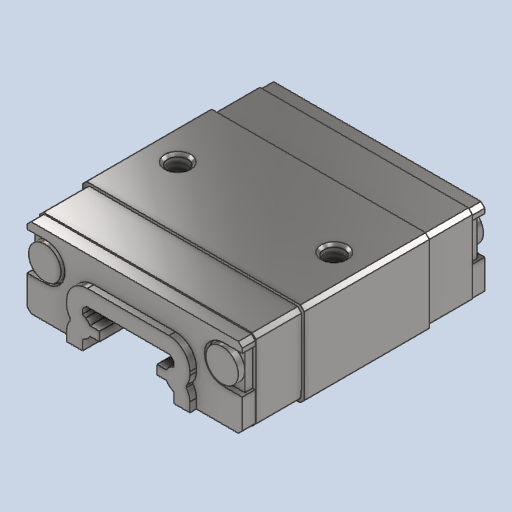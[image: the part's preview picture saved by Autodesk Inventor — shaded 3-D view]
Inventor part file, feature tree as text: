
AUTODESK INVENTOR PART (.ipt)
format: ipt  version: 2023 (Build 270158000, 158)  size: 541,184 bytes
history: native  units: mm
features: sketch x21, extrude x16, other x7, revolve x4, hole x1, pattern_linear x1
ambient origin geometry x8: Origin, YZ Plane, XZ Plane, XY Plane, X Axis, Y Axis, Z Axis, Center Point
bodies: Solid1 (feature_tree)
feature tree (50):
  extrude  "Extrusion1"  Depth=5.0mm TaperAngle=0.0deg
  extrude  "Extrusion2"  Depth=1.5mm TaperAngle=0.0deg
  extrude  "Extrusion3"  Depth=1.5mm TaperAngle=0.0deg
  extrude  "Extrusion4"  Depth=0.6mm TaperAngle=0.0deg
  extrude  "Extrusion5"  Depth=0.6mm TaperAngle=0.0deg
  extrude  "Extrusion6"  TaperAngle=360.0deg  [1 undecoded]
  extrude  "Extrusion7"  TaperAngle=360.0deg  [1 undecoded]
  extrude  "Extrusion8"  Depth=9.6mm TaperAngle=0.0deg
  extrude  "Extrusion9"  Depth=0.05mm TaperAngle=0.0deg
  extrude  "Extrusion10"  Depth=0.05mm TaperAngle=0.0deg
  extrude  "Extrusion11"  Depth=12.0mm TaperAngle=0.0deg
  revolve  "Revolution1"  [1 undecoded]
  revolve  "Revolution2"  [1 undecoded]
  revolve  "Revolution3"  [1 undecoded]
  revolve  "Revolution4"  [1 undecoded]
  extrude  "Extrusion12"  [1 undecoded]
  extrude  "Extrusion13"  [1 undecoded]
  extrude  "Extrusion14"  [1 undecoded]
  extrude  "Extrusion15"  [1 undecoded]
  extrude  "Extrusion16"  [1 undecoded]
  hole  "Hole1"  [1 undecoded]
  pattern_linear  "Rectangular Pattern1"  [2 undecoded]
  other  "to_rail_XY"
  other  "to_rail_YZ"
  other  "to_rail_ZX"
  other  "to_rail_X"
  other  "to_rail_Y"
  other  "to_rail_Z"
  other  "to_rail_Center"
  sketch  "Sketch_1"  dims[d0=9.6mm d1=0.0mm d2=5.0mm d3=0.0mm]
  sketch  "Sketch_3"  dims[d4=5.0mm d5=0.0mm d6=1.5mm d7=0.0mm]
  sketch  "Sketch_4"  dims[d8=0.5mm d9=0.0mm d10=1.5mm d11=0.0mm]
  sketch  "Sketch_8"  dims[d23=360.0deg d24=360.0deg]
  sketch  "Sketch_6"  dims[d16=0.6mm d17=0.0mm d18=0.6mm d19=0.0mm]
  sketch  "Sketch_7"  dims[d20=0.6mm d21=0.0mm d22=360.0deg]
  sketch  "Sketch_12"  dims[d36=1.567mm d37=2.5mm d38=2.0mm d39=2.0mm d40=90.0deg d41=5.5mm d42=120.0deg d43=20.0mm d45=12.0mm d46=10.0mm d48=0.0mm]
  sketch  "Sketch_25"
  sketch  "Sketch_5"  dims[d12=0.5mm d13=0.0mm d14=0.6mm d15=0.0mm]
  sketch  "Sketch_9"  dims[d25=360.0deg d26=9.6mm d27=0.0mm]
  sketch  "Sketch_26"
  sketch  "Sketch_18"
  sketch  "Sketch_19"
  sketch  "Sketch_20"
  sketch  "Sketch_21"
  sketch  "Sketch_17"
  sketch  "Sketch_11"  dims[d32=9.6mm d33=0.0mm d34=0.05mm d35=0.0mm]
  sketch  "Sketch_22"
  sketch  "Sketch_10"  dims[d28=9.6mm d29=0.0mm d30=0.05mm d31=0.0mm]
  sketch  "Sketch_23"
  sketch  "Sketch21"
note: 14 required parameter values undecoded (feature->parameter linkage not recoverable at this tier; creation-order binding heuristic only, values carry confidence <= 0.55)
